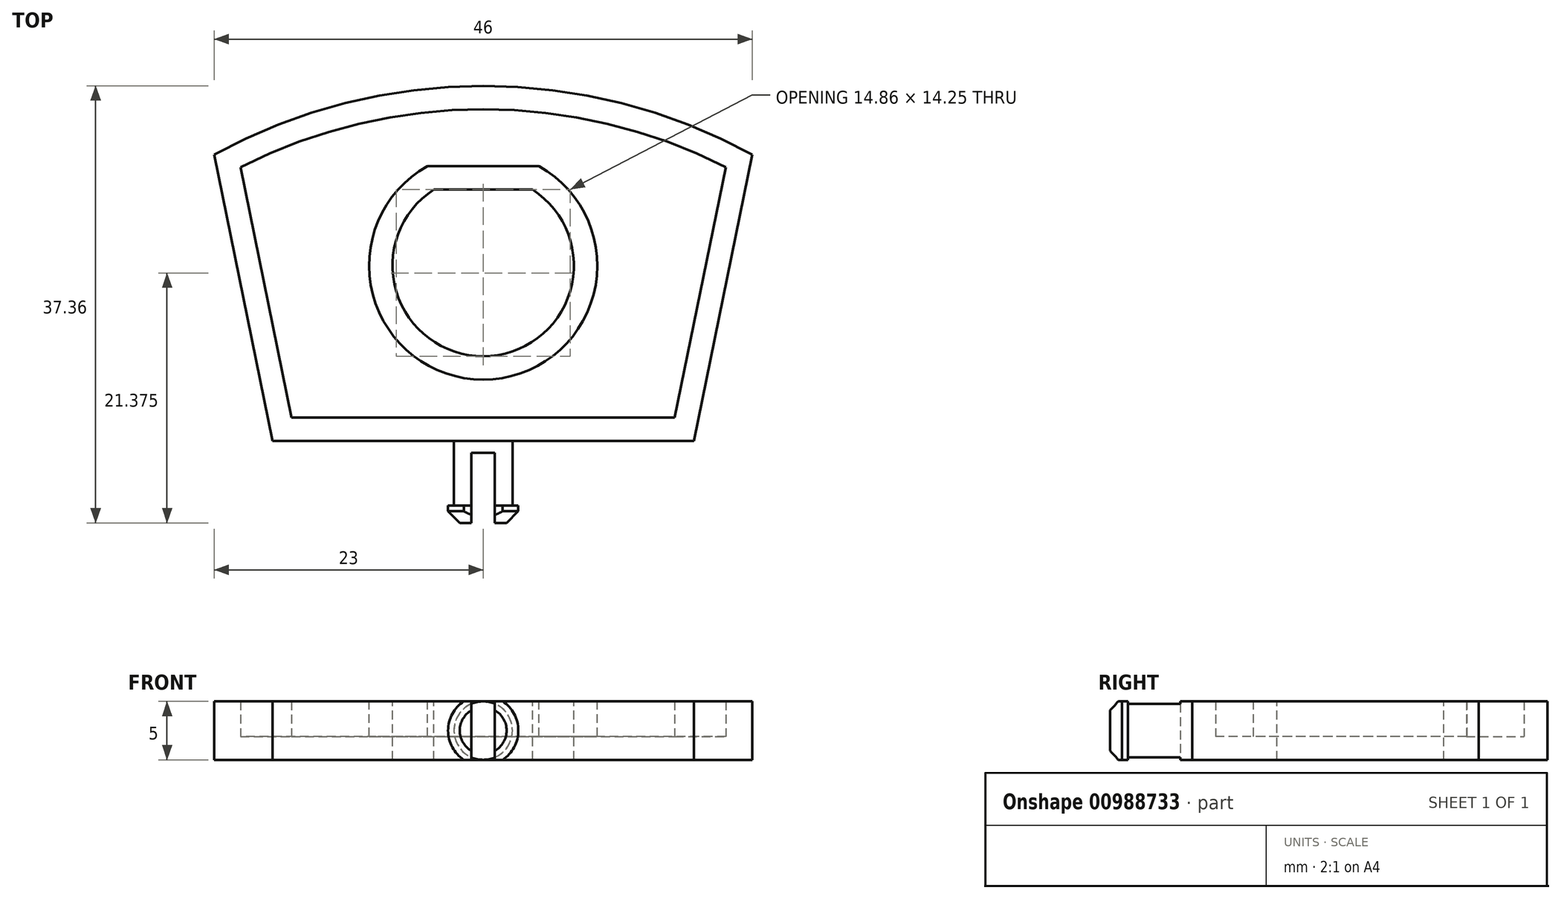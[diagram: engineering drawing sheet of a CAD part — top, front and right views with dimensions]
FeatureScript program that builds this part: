
annotation { "Feature Type Name" : "Feature", "Feature Type Description" : "" }
export const myFeature = defineFeature(function(context is Context, id is Id, definition is map)
    precondition{}
    {
        {
            var Q0;
            Q0=qCreatedBy(makeId("Top.planeOp"),FACE);
            var sketch = newSketch(context, id + "F0", { "sketchPlane" : qUnion([Q0])});
            skLineSegment(sketch, "E0", {"start": v(-23, 24.5) * mm, "end": v(-18, 0) * mm});
            skLineSegment(sketch, "E1", {"start": v(-18, 0) * mm, "end": v(18, 0) * mm});
            skLineSegment(sketch, "E2", {"start": v(18, 0) * mm, "end": v(23, 24.5) * mm});
            skArc(sketch, "E3", {"start": v(23, 24.5) * mm, "mid": v(0, 30.36) * mm, "end": v(-23, 24.5) * mm});
            skSolve(sketch);
        }
        {
            var Q0;
            Q0=makeQuery(id+"F0.imprint","IMPRINT",FACE,{"disambiguationData":[TD([[makeQuery(id+"F0.imprint","IMPRINT",EDGE,{"derivedFrom":sQuery(id+"F0.wireOp",EDGE,"E0")}),1.0]])]});
            extrude(context, id + "F1", {"entities" : qUnion([Q0]), "endBound" : BoundingType.SYMMETRIC, "depth" : 5 * mm, "offsetDistance" : 25 * mm});
        }
        {
            var Q0;
            Q0=makeQuery(id+"F1.opExtrude","CAP_FACE",FACE,{"disambiguationData":[OSD([sQuery(id+"F0.wireOp",EDGE,"E0"),sQuery(id+"F0.wireOp",EDGE,"E1"),sQuery(id+"F0.wireOp",EDGE,"E2"),sQuery(id+"F0.wireOp",EDGE,"E3")])],"isStart":false});
            var sketch = newSketch(context, id + "F2", { "sketchPlane" : qUnion([Q0])});
            skLineSegment(sketch, "E4", {"start": v(-4.22, 21.5) * mm, "end": v(4.22, 21.5) * mm});
            skArc(sketch, "E5", {"start": v(-4.22, 21.5) * mm, "mid": v(0, 7.25) * mm, "end": v(4.22, 21.5) * mm});
            skSolve(sketch);
        }
        {
            var Q0;
            Q0 = qSketchRegion(id + "F2", true);
            extrude(context, id + "F3", {"entities" : qUnion([Q0]), "operationType" : NewBodyOperationType.REMOVE, "endBound" : BoundingType.UP_TO_NEXT, "oppositeDirection" : true, "depth" : 25 * mm, "offsetDistance" : 25 * mm});
        }
        {
            var Q0;
            Q0=makeQuery(id+"F1.opExtrude","CAP_FACE",FACE,{"disambiguationData":[OSD([sQuery(id+"F0.wireOp",EDGE,"E0"),sQuery(id+"F0.wireOp",EDGE,"E1"),sQuery(id+"F0.wireOp",EDGE,"E2"),sQuery(id+"F0.wireOp",EDGE,"E3")])],"isStart":false});
            shell(context, id + "F4", {"entities" : qUnion([Q0]), "thickness" : 2 * mm});
        }
        {
            var Q0;
            Q0=qCreatedBy(makeId("Right.planeOp"),FACE);
            var sketch = newSketch(context, id + "F5", { "sketchPlane" : qUnion([Q0])});
            skLineSegment(sketch, "E6", {"start": v(0, 0) * mm, "end": v(-7, 0) * mm});
            skLineSegment(sketch, "E7", {"start": v(-7, 0) * mm, "end": v(-7, 3) * mm});
            skLineSegment(sketch, "E8", {"start": v(-7, 3) * mm, "end": v(-5.5, 3) * mm});
            skLineSegment(sketch, "E9", {"start": v(-5.5, 3) * mm, "end": v(-5.5, 2.5) * mm});
            skLineSegment(sketch, "E10", {"start": v(-5.5, 2.5) * mm, "end": v(0, 2.5) * mm});
            skLineSegment(sketch, "E11", {"start": v(0, 2.5) * mm, "end": v(0, 0) * mm});
            skSolve(sketch);
        }
        {
            var Q0;
            Q0=makeQuery(id+"F5.imprint","IMPRINT",FACE,{"disambiguationData":[TD([[makeQuery(id+"F5.imprint","IMPRINT",EDGE,{"derivedFrom":sQuery(id+"F5.wireOp",EDGE,"E6")}),-1.0]])]});
            var Q1;
            Q1=sQuery(id+"F5.wireOp",EDGE,"E6");
            revolve(context, id + "F6", {"operationType" : NewBodyOperationType.ADD, "surfaceOperationType" : NewSurfaceOperationType.NEW, "entities" : qUnion([Q0]), "axis" : qUnion([Q1]), "revolveType" : RevolveType.FULL});
        }
        {
            var Q0;
            Q0=makeQuery(id+"F6.opRevolve","SWEPT_EDGE",EDGE,{"disambiguationData":[OSD([sQuery(id+"F5.wireOp",EDGE,"E7"),sQuery(id+"F5.wireOp",EDGE,"E8")])]});
            chamfer(context, id + "F7", {"entities" : qUnion([Q0]), "width" : 1 * mm, "tangentPropagation" : true});
        }
        {
            var Q0;
            Q0=qCreatedBy(makeId("Front.planeOp"),FACE);
            var sketch = newSketch(context, id + "F8", { "sketchPlane" : qUnion([Q0])});
            skLineSegment(sketch, "E12.bottom", {"start": v(-8.3, 6.36) * mm, "end": v(8.3, 6.36) * mm});
            skLineSegment(sketch, "E12.top", {"start": v(-8.3, 2.5) * mm, "end": v(8.3, 2.5) * mm});
            skLineSegment(sketch, "E12.left", {"start": v(-8.3, 6.36) * mm, "end": v(-8.3, 2.5) * mm});
            skLineSegment(sketch, "E12.right", {"start": v(8.3, 6.36) * mm, "end": v(8.3, 2.5) * mm});
            skLineSegment(sketch, "E13.bottom", {"start": v(-8.3, -2.5) * mm, "end": v(8.3, -2.5) * mm});
            skLineSegment(sketch, "E13.top", {"start": v(-8.3, -6.82) * mm, "end": v(8.3, -6.82) * mm});
            skLineSegment(sketch, "E13.left", {"start": v(-8.3, -2.5) * mm, "end": v(-8.3, -6.82) * mm});
            skLineSegment(sketch, "E13.right", {"start": v(8.3, -2.5) * mm, "end": v(8.3, -6.82) * mm});
            skSolve(sketch);
        }
        {
            var Q0;
            Q0 = qSketchRegion(id + "F8", true);
            extrude(context, id + "F9", {"entities" : qUnion([Q0]), "operationType" : NewBodyOperationType.REMOVE, "depth" : 25 * mm, "offsetDistance" : 25 * mm});
        }
        {
            var Q0;
            Q0=qCreatedBy(makeId("Front.planeOp"),FACE);
            cPlane(context, id + "F10", {"entities" : qUnion([Q0]), "cplaneType" : CPlaneType.OFFSET, "offset" : 7 * mm, "width" : 150 * mm, "height" : 150 * mm});
        }
        {
            var Q0;
            Q0=qCreatedBy(id+"F10.planeOp",FACE);
            var sketch = newSketch(context, id + "F11", { "sketchPlane" : qUnion([Q0])});
            skLineSegment(sketch, "E14.bottom", {"start": v(-1, 5) * mm, "end": v(1, 5) * mm});
            skLineSegment(sketch, "E14.top", {"start": v(-1, -3.65) * mm, "end": v(1, -3.65) * mm});
            skLineSegment(sketch, "E14.left", {"start": v(-1, 5) * mm, "end": v(-1, -3.65) * mm});
            skLineSegment(sketch, "E14.right", {"start": v(1, 5) * mm, "end": v(1, -3.65) * mm});
            skSolve(sketch);
        }
        {
            var Q0;
            Q0 = qSketchRegion(id + "F11", true);
            extrude(context, id + "F12", {"entities" : qUnion([Q0]), "operationType" : NewBodyOperationType.REMOVE, "oppositeDirection" : true, "depth" : 6 * mm, "offsetDistance" : 25 * mm});
        }
    });
